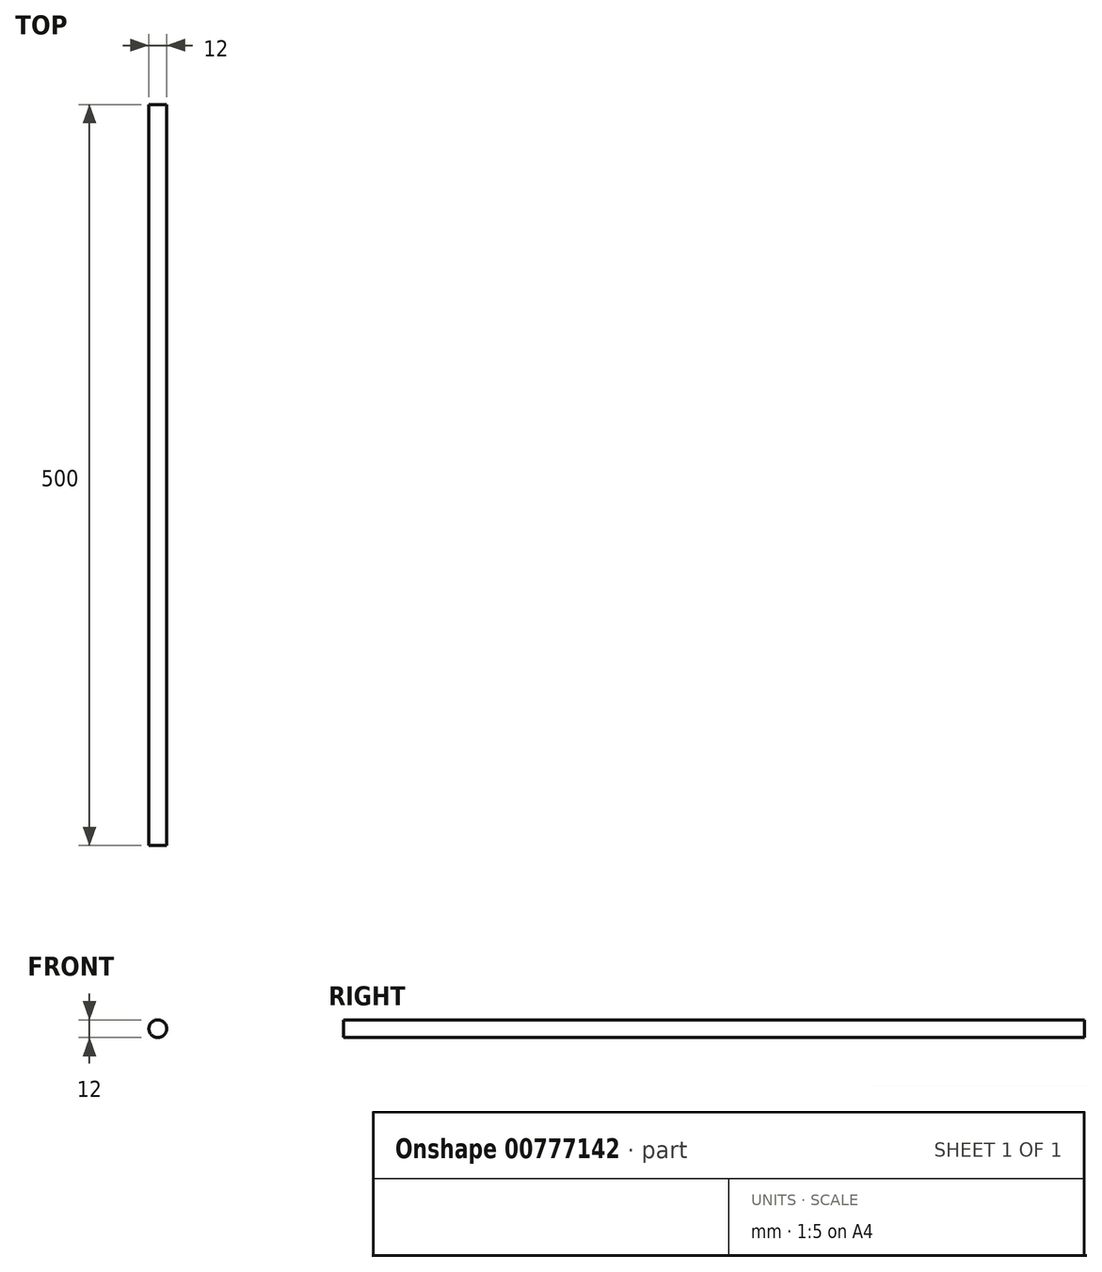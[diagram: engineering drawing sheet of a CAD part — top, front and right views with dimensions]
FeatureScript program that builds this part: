
annotation { "Feature Type Name" : "Feature", "Feature Type Description" : "" }
export const myFeature = defineFeature(function(context is Context, id is Id, definition is map)
    precondition{}
    {
        {
            var Q0;
            Q0=qCreatedBy(makeId("Front.planeOp"),FACE);
            var sketch = newSketch(context, id + "F0", { "sketchPlane" : qUnion([Q0])});
            skCircle(sketch, "E0", {"center": v(0, 0) * mm, "radius": 6 * mm});
            skSolve(sketch);
        }
        {
            var Q0;
            Q0 = qSketchRegion(id + "F0", true);
            extrude(context, id + "F1", {"entities" : qUnion([Q0]), "depth" : 500 * mm, "offsetDistance" : 25 * mm});
        }
    });
